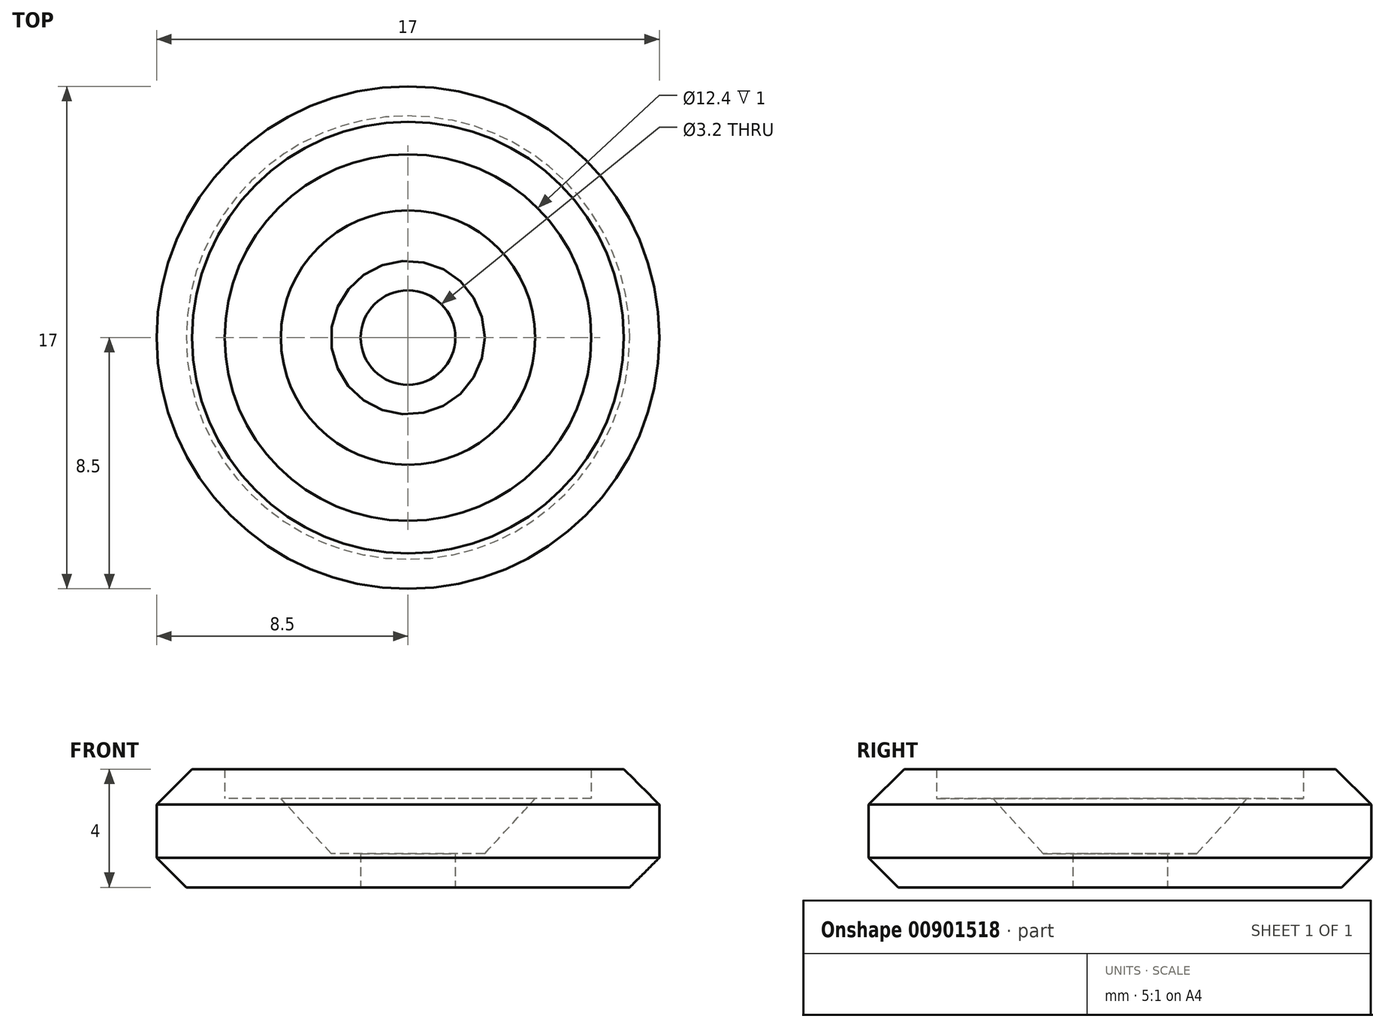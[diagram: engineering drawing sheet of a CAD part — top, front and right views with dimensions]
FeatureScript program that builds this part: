
annotation { "Feature Type Name" : "Feature", "Feature Type Description" : "" }
export const myFeature = defineFeature(function(context is Context, id is Id, definition is map)
    precondition{}
    {
        {
            var Q0;
            Q0=qCreatedBy(makeId("Top.planeOp"),FACE);
            var sketch = newSketch(context, id + "F0", { "sketchPlane" : qUnion([Q0])});
            skCircle(sketch, "E0", {"center": v(0, 0) * mm, "radius": 8.5 * mm});
            skSolve(sketch);
        }
        {
            var Q0;
            Q0=makeQuery(id+"F0.imprint","IMPRINT",FACE,{"disambiguationData":[TD([[makeQuery(id+"F0.imprint","IMPRINT",EDGE,{"derivedFrom":sQuery(id+"F0.wireOp",EDGE,"E0")}),1.0]])]});
            extrude(context, id + "F1", {"entities" : qUnion([Q0]), "depth" : 3 * mm, "offsetDistance" : 25 * mm});
        }
        {
            var Q0;
            Q0=makeQuery(id+"F1.opExtrude","CAP_FACE",FACE,{"disambiguationData":[OSD([sQuery(id+"F0.wireOp",EDGE,"E0")])],"isStart":false});
            var sketch = newSketch(context, id + "F2", { "sketchPlane" : qUnion([Q0])});
            skPoint(sketch, "E1", {"position": v(0, 0) * mm});
            skSolve(sketch);
        }
        {
            var Q0;
            Q0=sQuery(id+"F2.wireOp",VERTEX,"E1");
            var Q1;
            Q1=makeQuery(id+"F1.opExtrude","SWEPT_BODY",BODY,{"disambiguationData":[OSD([sQuery(id+"F0.wireOp",EDGE,"E0")])]});
            hole(context, id + "F3", {"style" : HoleStyle.C_SINK, "endStyle" : HoleEndStyle.THROUGH, "holeDiameter" : 5.2 * mm, "cSinkDiameter" : 8.6 * mm, "cSinkAngle" : 85 * degree, "majorDiameter" : 5 * mm, "isTappedThrough" : true, "tappedDepth" : 12 * mm, "tapClearance" : 3, "locations" : qUnion([Q0]), "scope" : qUnion([Q1])});
        }
        {
            var Q0;
            Q0=makeQuery(id+"F1.opExtrude","CAP_FACE",FACE,{"disambiguationData":[OSD([sQuery(id+"F0.wireOp",EDGE,"E0")])],"isStart":false});
            var sketch = newSketch(context, id + "F4", { "sketchPlane" : qUnion([Q0])});
            skPoint(sketch, "E2", {"position": v(0, 0) * mm});
            skCircle(sketch, "E3", {"center": v(0, 0) * mm, "radius": 8.5 * mm});
            skCircle(sketch, "E4", {"center": v(0, 0) * mm, "radius": 6.2 * mm});
            skSolve(sketch);
        }
        {
            var Q0;
            Q0=makeQuery(id+"F4.imprint","IMPRINT",FACE,{"disambiguationData":[TD([[makeQuery(id+"F4.imprint","IMPRINT",EDGE,{"derivedFrom":sQuery(id+"F4.wireOp",EDGE,"E3")}),1.0]])]});
            extrude(context, id + "F5", {"entities" : qUnion([Q0]), "operationType" : NewBodyOperationType.ADD, "depth" : 1 * mm, "offsetDistance" : 25 * mm});
        }
        {
            var Q0;
            Q0=makeQuery(id+"F1.opExtrude","CAP_EDGE",EDGE,{"disambiguationData":[OSD([sQuery(id+"F0.wireOp",EDGE,"E0")])],"isStart":true});
            chamfer(context, id + "F6", {"entities" : qUnion([Q0]), "width" : 1 * mm, "tangentPropagation" : true});
        }
        {
            var Q0;
            Q0=makeQuery(id+"F5.opExtrude","CAP_EDGE",EDGE,{"disambiguationData":[OSD([sQuery(id+"F4.wireOp",EDGE,"E3")])],"isStart":false});
            chamfer(context, id + "F7", {"entities" : qUnion([Q0]), "width" : 1.2 * mm, "tangentPropagation" : true});
        }
        {
            var Q0;
            Q0=makeQuery(id+"F1.opExtrude","CAP_FACE",FACE,{"disambiguationData":[OSD([sQuery(id+"F0.wireOp",EDGE,"E0")])],"isStart":true});
            var sketch = newSketch(context, id + "F8", { "sketchPlane" : qUnion([Q0])});
            skCircle(sketch, "E5", {"center": v(0, 0) * mm, "radius": 2.6 * mm});
            skCircle(sketch, "E6", {"center": v(0, 0) * mm, "radius": 1.6 * mm});
            skSolve(sketch);
        }
        {
            var Q0;
            Q0=makeQuery(id+"F8.imprint","IMPRINT",FACE,{"disambiguationData":[TD([[makeQuery(id+"F8.imprint","IMPRINT",EDGE,{"derivedFrom":sQuery(id+"F8.wireOp",EDGE,"E5")}),1.0]])]});
            extrude(context, id + "F9", {"entities" : qUnion([Q0]), "operationType" : NewBodyOperationType.ADD, "oppositeDirection" : true, "depth" : 1.14 * mm, "offsetDistance" : 25 * mm});
        }
    });
